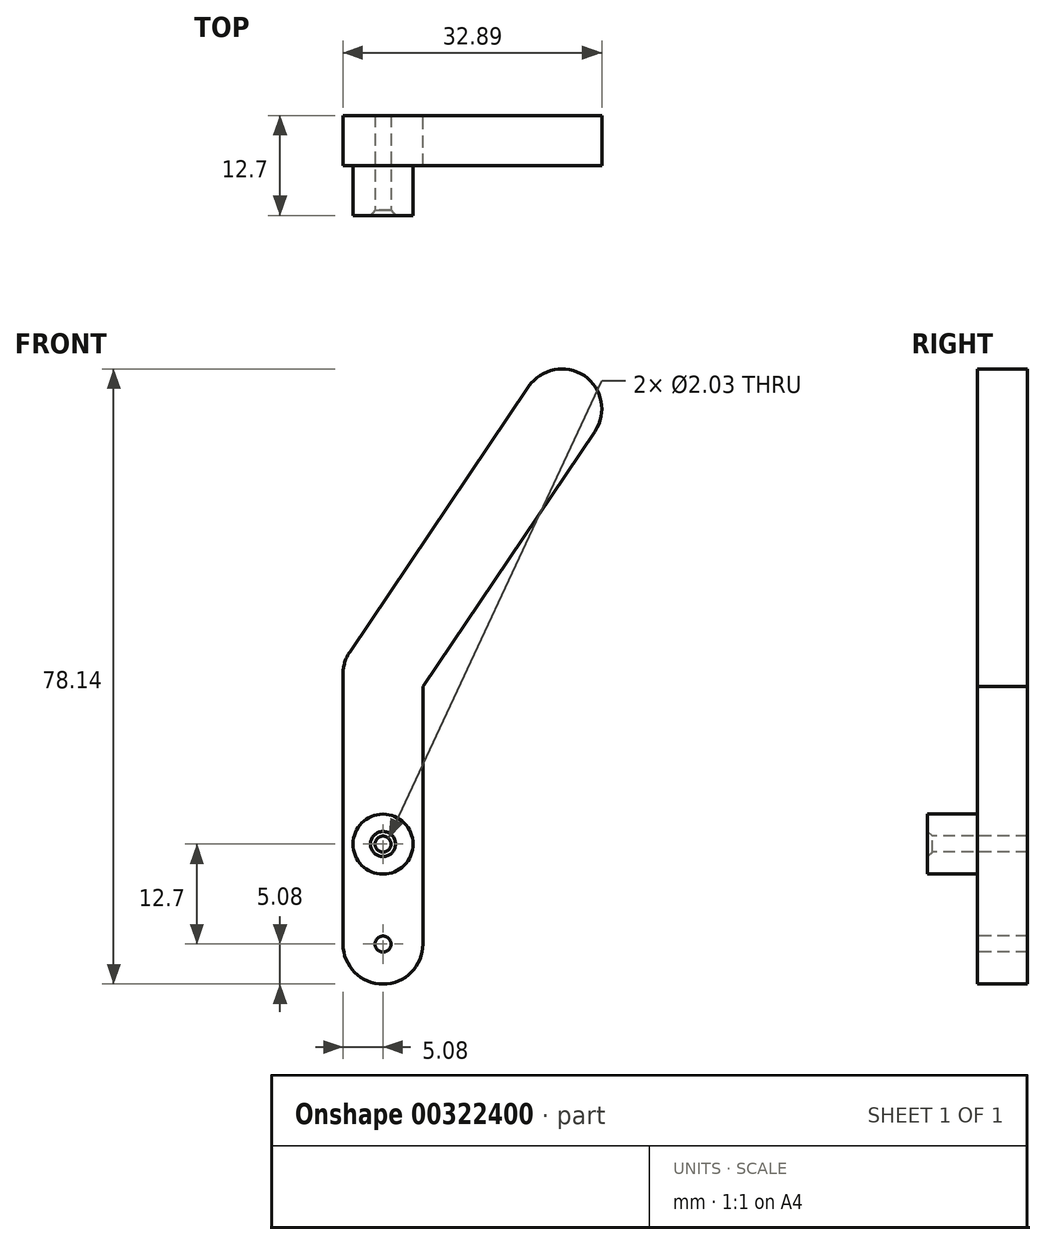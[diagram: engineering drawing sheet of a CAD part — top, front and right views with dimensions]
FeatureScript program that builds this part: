
annotation { "Feature Type Name" : "Feature", "Feature Type Description" : "" }
export const myFeature = defineFeature(function(context is Context, id is Id, definition is map)
    precondition{}
    {
        {
            var Q0;
            Q0=qCreatedBy(makeId("Front.planeOp"),FACE);
            var sketch = newSketch(context, id + "F0", { "sketchPlane" : qUnion([Q0])});
            skLineSegment(sketch, "E0", {"start": v(0, 0) * mm, "end": v(0, 12.7) * mm});
            skLineSegment(sketch, "E1", {"start": v(0, 12.7) * mm, "end": v(0, 34.3) * mm});
            skLineSegment(sketch, "E2", {"start": v(0, 34.3) * mm, "end": v(22.73, 67.98) * mm});
            skArc(sketch, "E3.0.startCap", {"start": v(5.08, 0) * mm, "mid": v(0, -5.08) * mm, "end": v(-5.08, 0) * mm});
            skArc(sketch, "E3.0.endCap", {"start": v(-5.08, 12.7) * mm, "mid": v(0, 17.78) * mm, "end": v(5.08, 12.7) * mm});
            skLineSegment(sketch, "E3.0.left", {"start": v(-5.08, 0) * mm, "end": v(-5.08, 12.7) * mm});
            skLineSegment(sketch, "E3.0.right", {"start": v(5.08, 0) * mm, "end": v(5.08, 12.7) * mm});
            skArc(sketch, "E3.1.startCap", {"start": v(5.08, 12.7) * mm, "mid": v(0, 7.62) * mm, "end": v(-5.08, 12.7) * mm});
            skArc(sketch, "E3.1.endCap", {"start": v(-5.08, 34.3) * mm, "mid": v(0, 39.37) * mm, "end": v(5.08, 34.3) * mm});
            skLineSegment(sketch, "E3.1.left", {"start": v(-5.08, 12.7) * mm, "end": v(-5.08, 34.3) * mm});
            skLineSegment(sketch, "E3.1.right", {"start": v(5.08, 12.7) * mm, "end": v(5.08, 34.3) * mm});
            skArc(sketch, "E3.2.startCap", {"start": v(4.21, 31.45) * mm, "mid": v(-2.84, 30.08) * mm, "end": v(-4.21, 37.13) * mm});
            skArc(sketch, "E3.2.endCap", {"start": v(18.51, 70.82) * mm, "mid": v(25.57, 72.2) * mm, "end": v(26.94, 65.14) * mm});
            skLineSegment(sketch, "E3.2.left", {"start": v(-4.21, 37.13) * mm, "end": v(18.51, 70.82) * mm});
            skLineSegment(sketch, "E3.2.right", {"start": v(4.21, 31.45) * mm, "end": v(26.94, 65.14) * mm});
            skSolve(sketch);
        }
        {
            var Q0;
            Q0 = qSketchRegion(id + "F0", true);
            extrude(context, id + "F1", {"entities" : qUnion([Q0]), "depth" : 6.35 * mm});
        }
        {
            var Q0;
            Q0=makeQuery(id+"F1.opExtrude","CAP_FACE",FACE,{"disambiguationData":[OSD([sQuery(id+"F0.wireOp",EDGE,"E3.0.startCap"),sQuery(id+"F0.wireOp",EDGE,"E3.0.left"),sQuery(id+"F0.wireOp",EDGE,"E3.0.right"),sQuery(id+"F0.wireOp",EDGE,"E3.1.left"),sQuery(id+"F0.wireOp",EDGE,"E3.1.right"),sQuery(id+"F0.wireOp",EDGE,"E3.2.startCap"),sQuery(id+"F0.wireOp",EDGE,"E3.2.endCap"),sQuery(id+"F0.wireOp",EDGE,"E3.2.left"),sQuery(id+"F0.wireOp",EDGE,"E3.2.right")])],"isStart":false});
            var sketch = newSketch(context, id + "F2", { "sketchPlane" : qUnion([Q0])});
            skLineSegment(sketch, "E4", {"start": v(0, 0) * mm, "end": v(0, 12.7) * mm});
            skCircle(sketch, "E5", {"center": v(0, 12.7) * mm, "radius": 3.81 * mm});
            skSolve(sketch);
        }
        {
            var Q0;
            Q0 = qSketchRegion(id + "F2", true);
            extrude(context, id + "F3", {"entities" : qUnion([Q0]), "operationType" : NewBodyOperationType.ADD, "depth" : 6.35 * mm});
        }
        {
            var Q0;
            Q0=makeQuery(id+"F3.opExtrude","CAP_FACE",FACE,{"disambiguationData":[OSD([sQuery(id+"F2.wireOp",EDGE,"E5")])],"isStart":false});
            var sketch = newSketch(context, id + "F4", { "sketchPlane" : qUnion([Q0])});
            skPoint(sketch, "E6", {"position": v(0, 12.7) * mm});
            skSolve(sketch);
        }
        {
            var Q0;
            Q0=sQuery(id+"F4.wireOp",VERTEX,"E6");
            var Q1;
            Q1=makeQuery(id+"F1.opExtrude","SWEPT_BODY",BODY,{"disambiguationData":[OSD([sQuery(id+"F0.wireOp",EDGE,"E3.0.startCap"),sQuery(id+"F0.wireOp",EDGE,"E3.0.left"),sQuery(id+"F0.wireOp",EDGE,"E3.0.right"),sQuery(id+"F0.wireOp",EDGE,"E3.1.left"),sQuery(id+"F0.wireOp",EDGE,"E3.1.right"),sQuery(id+"F0.wireOp",EDGE,"E3.2.startCap"),sQuery(id+"F0.wireOp",EDGE,"E3.2.endCap"),sQuery(id+"F0.wireOp",EDGE,"E3.2.left"),sQuery(id+"F0.wireOp",EDGE,"E3.2.right")])]});
            hole(context, id + "F5", {"style" : HoleStyle.C_SINK, "endStyle" : HoleEndStyle.THROUGH, "holeDiameter" : 2.03 * mm, "cSinkDiameter" : 3.17 * mm, "cSinkAngle" : 82 * degree, "tappedDepth" : 12.7 * mm, "tapClearance" : 3, "locations" : qUnion([Q0]), "scope" : qUnion([Q1])});
        }
        {
            var Q0;
            Q0=makeQuery(id+"F1.opExtrude","CAP_FACE",FACE,{"disambiguationData":[OSD([sQuery(id+"F0.wireOp",EDGE,"E3.0.startCap"),sQuery(id+"F0.wireOp",EDGE,"E3.0.left"),sQuery(id+"F0.wireOp",EDGE,"E3.0.right"),sQuery(id+"F0.wireOp",EDGE,"E3.1.left"),sQuery(id+"F0.wireOp",EDGE,"E3.1.right"),sQuery(id+"F0.wireOp",EDGE,"E3.2.startCap"),sQuery(id+"F0.wireOp",EDGE,"E3.2.endCap"),sQuery(id+"F0.wireOp",EDGE,"E3.2.left"),sQuery(id+"F0.wireOp",EDGE,"E3.2.right")])],"isStart":false});
            var sketch = newSketch(context, id + "F6", { "sketchPlane" : qUnion([Q0])});
            skPoint(sketch, "E7", {"position": v(0, 0) * mm});
            skSolve(sketch);
        }
        {
            var Q0;
            Q0=sQuery(id+"F6.wireOp",VERTEX,"E7");
            var Q1;
            Q1=makeQuery(id+"F1.opExtrude","SWEPT_BODY",BODY,{"disambiguationData":[OSD([sQuery(id+"F0.wireOp",EDGE,"E3.0.startCap"),sQuery(id+"F0.wireOp",EDGE,"E3.0.left"),sQuery(id+"F0.wireOp",EDGE,"E3.0.right"),sQuery(id+"F0.wireOp",EDGE,"E3.1.left"),sQuery(id+"F0.wireOp",EDGE,"E3.1.right"),sQuery(id+"F0.wireOp",EDGE,"E3.2.startCap"),sQuery(id+"F0.wireOp",EDGE,"E3.2.endCap"),sQuery(id+"F0.wireOp",EDGE,"E3.2.left"),sQuery(id+"F0.wireOp",EDGE,"E3.2.right")])]});
            hole(context, id + "F7", {"style" : HoleStyle.SIMPLE, "endStyle" : HoleEndStyle.THROUGH, "holeDiameter" : 2.03 * mm, "tappedDepth" : 12.7 * mm, "tapClearance" : 3, "locations" : qUnion([Q0]), "scope" : qUnion([Q1])});
        }
    });
